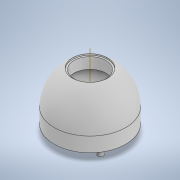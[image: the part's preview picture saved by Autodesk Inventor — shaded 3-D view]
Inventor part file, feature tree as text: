
AUTODESK INVENTOR PART (.ipt)
format: ipt  version: 2021 (Build 250183000, 183)  size: 419,328 bytes
history: native  units: in
note: dims shown in document units (in); Inventor stores cm internally (conversion verified against a paired STEP export)
features: sketch x6, extrude x5, other x1, revolve x1, pattern_circular x1, mirror x1, fillet x1
ambient origin geometry x8: Origin, YZ Plane, XZ Plane, XY Plane, X Axis, Y Axis, Z Axis, Center Point
bodies: Solid1 (feature_tree)
feature tree (16):
  extrude  "Extrusion1"  Depth=1.0236in
  other  "Work Axis1"
  revolve  "Revolution1"  [1 undecoded]
  extrude  "Extrusion2"  Depth=1.0079in
  extrude  "Extrusion3"  TaperAngle=90.0deg  [1 undecoded]
  extrude  "Extrusion4"  Depth=0.9134in
  extrude  "Extrusion5"  Depth=1.0236in TaperAngle=0.0deg
  pattern_circular  "Circular Pattern1"  [2 undecoded]
  mirror  "Mirror1"
  fillet  "Fillet2"  Radius=0.1654in
  sketch  "Sketch1"  dims[d0=2.0472in d1=1.0236in]
  sketch  "Sketch2"  dims[d2=1.0236in d3=1.0236in]
  sketch  "Sketch3"  dims[d4=1.378in d5=0.0in d6=1.0079in]
  sketch  "Sketch4"  dims[d7=90.0deg d8=90.0deg]
  sketch  "Sketch5"  dims[d9=0.0394in d10=0.0in d11=0.9134in]
  sketch  "Sketch8"  dims[d12=0.0in d13=0.0in d14=1.0236in d15=0.0in d16=1.2913in d21=0.1654in d22=0.8268in d23=0.1969in d24=0.0in d25=1.9685in d26=240.0deg d33=0.5039in d34=0.0394in]
note: 4 required parameter values undecoded (feature->parameter linkage not recoverable at this tier; creation-order binding heuristic only, values carry confidence <= 0.55)